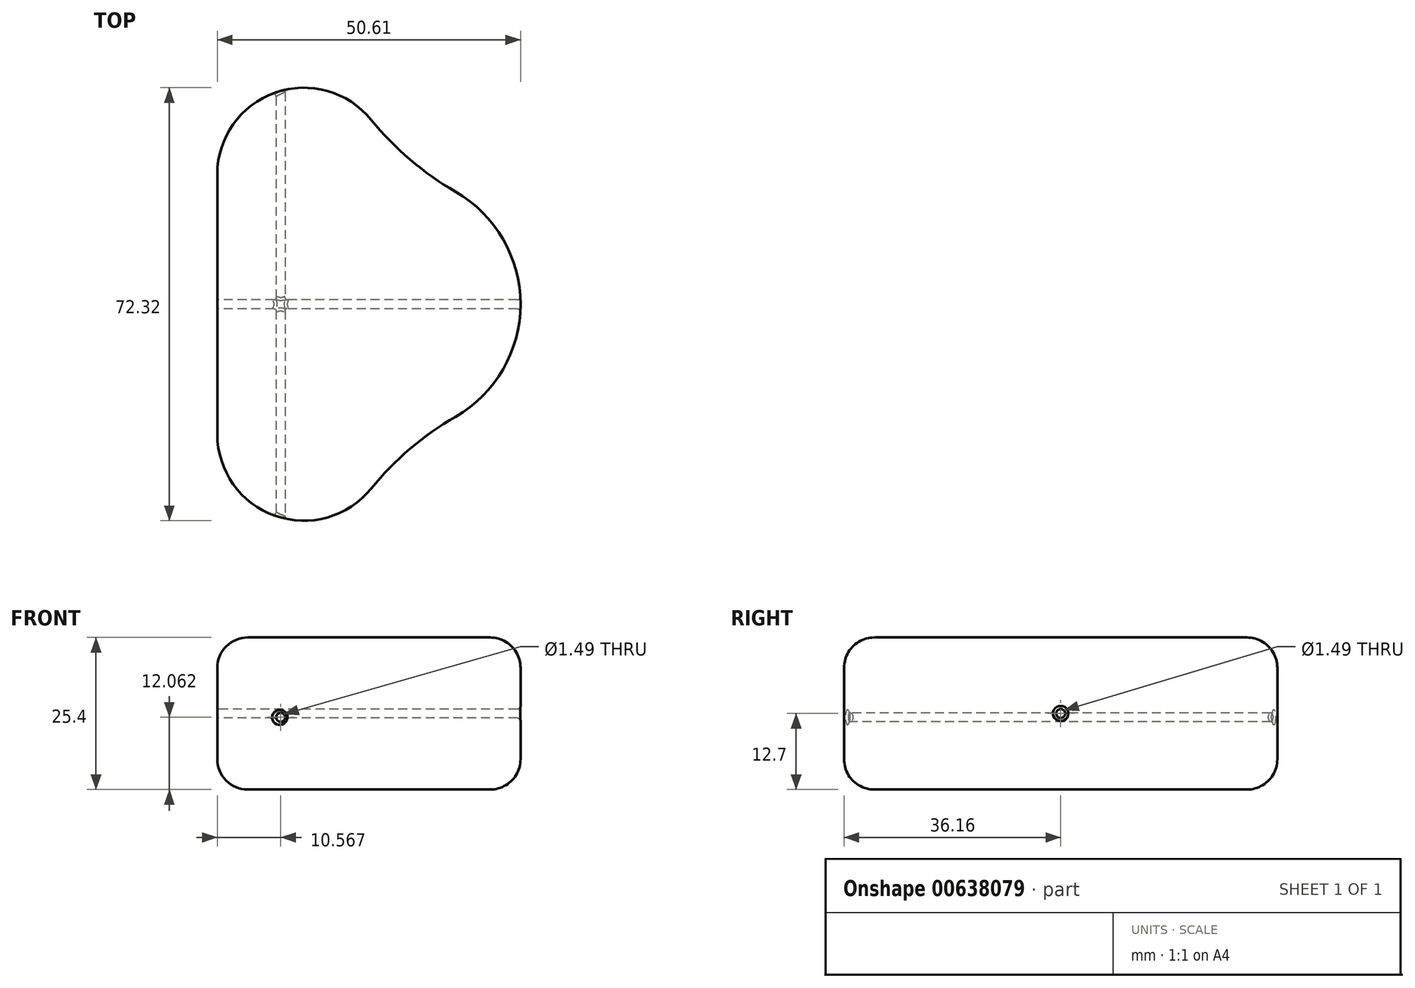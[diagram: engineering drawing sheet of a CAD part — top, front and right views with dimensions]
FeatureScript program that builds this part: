
annotation { "Feature Type Name" : "Feature", "Feature Type Description" : "" }
export const myFeature = defineFeature(function(context is Context, id is Id, definition is map)
    precondition{}
    {
        {
            var Q0;
            Q0=qCreatedBy(makeId("Top.planeOp"),FACE);
            var sketch = newSketch(context, id + "F0", { "sketchPlane" : qUnion([Q0])});
            skLineSegment(sketch, "E0.bottom", {"start": v(-14.45, -21.7) * mm, "end": v(14.45, -21.7) * mm});
            skLineSegment(sketch, "E0.top", {"start": v(-14.45, 21.7) * mm, "end": v(14.45, 21.7) * mm});
            skLineSegment(sketch, "E0.left", {"start": v(-14.45, -21.7) * mm, "end": v(-14.45, 21.7) * mm});
            skLineSegment(sketch, "E0.right", {"start": v(14.45, -21.7) * mm, "end": v(14.45, 21.7) * mm});
            skPoint(sketch, "E0.middle", {"position": v(0, 0) * mm});
            skCircle(sketch, "E1", {"center": v(0, -21.7) * mm, "radius": 14.45 * mm});
            skCircle(sketch, "E2", {"center": v(0, 21.7) * mm, "radius": 14.45 * mm});
            skCircle(sketch, "E3", {"center": v(14.45, 0) * mm, "radius": 21.7 * mm});
            skSolve(sketch);
        }
        {
            var Q0;
            {var subQ0=sQuery(id+"F0.wireOp",EDGE,"E0.top");Q0=makeQuery(id+"F0.imprint","IMPRINT",FACE,{"disambiguationData":[TD([[makeQuery(id+"F0.imprint","IMPRINT",EDGE,{"derivedFrom":subQ0}),1.0]])]});}
            var Q1;
            {var subQ0=sQuery(id+"F0.wireOp",EDGE,"E0.top");Q1=makeQuery(id+"F0.imprint","IMPRINT",FACE,{"disambiguationData":[TD([[makeQuery(id+"F0.imprint","IMPRINT",EDGE,{"derivedFrom":subQ0}),-1.0]])]});}
            var Q2;
            {var subQ0=sQuery(id+"F0.wireOp",EDGE,"E3");var subQ1=sQuery(id+"F0.wireOp",EDGE,"E2");var subQ3=makeQuery(id+"F0.imprint","INTERSECT",VERTEX,{"derivedFrom":[subQ1,subQ0]});Q2=makeQuery(id+"F0.imprint","IMPRINT",FACE,{"disambiguationData":[TD([[makeQuery(id+"F0.imprint","IMPRINT",EDGE,{"disambiguationData":[TD([[subQ3,-1.0]])],"derivedFrom":subQ1}),1.0]])]});}
            var Q3;
            {var subQ0=sQuery(id+"F0.wireOp",EDGE,"E0.left");Q3=makeQuery(id+"F0.imprint","IMPRINT",FACE,{"disambiguationData":[TD([[makeQuery(id+"F0.imprint","IMPRINT",EDGE,{"derivedFrom":subQ0}),-1.0]])]});}
            var Q4;
            {var subQ0=sQuery(id+"F0.wireOp",EDGE,"E0.bottom");Q4=makeQuery(id+"F0.imprint","IMPRINT",FACE,{"disambiguationData":[TD([[makeQuery(id+"F0.imprint","IMPRINT",EDGE,{"derivedFrom":subQ0}),1.0]])]});}
            var Q5;
            {var subQ0=sQuery(id+"F0.wireOp",EDGE,"E0.right");Q5=makeQuery(id+"F0.imprint","IMPRINT",FACE,{"disambiguationData":[TD([[makeQuery(id+"F0.imprint","IMPRINT",EDGE,{"derivedFrom":subQ0}),1.0]])]});}
            var Q6;
            {var subQ0=sQuery(id+"F0.wireOp",EDGE,"E0.right");Q6=makeQuery(id+"F0.imprint","IMPRINT",FACE,{"disambiguationData":[TD([[makeQuery(id+"F0.imprint","IMPRINT",EDGE,{"derivedFrom":subQ0}),-1.0]])]});}
            var Q7;
            {var subQ0=sQuery(id+"F0.wireOp",EDGE,"E0.bottom");Q7=makeQuery(id+"F0.imprint","IMPRINT",FACE,{"disambiguationData":[TD([[makeQuery(id+"F0.imprint","IMPRINT",EDGE,{"derivedFrom":subQ0}),-1.0]])]});}
            var Q8;
            {var subQ0=sQuery(id+"F0.wireOp",EDGE,"E3");var subQ1=sQuery(id+"F0.wireOp",EDGE,"E1");var subQ3=makeQuery(id+"F0.imprint","INTERSECT",VERTEX,{"derivedFrom":[subQ1,subQ0]});Q8=makeQuery(id+"F0.imprint","IMPRINT",FACE,{"disambiguationData":[TD([[makeQuery(id+"F0.imprint","IMPRINT",EDGE,{"disambiguationData":[TD([[subQ3,1.0]])],"derivedFrom":subQ1}),1.0]])]});}
            extrude(context, id + "F1", {"entities" : qUnion([Q0, Q1, Q2, Q3, Q4, Q5, Q6, Q7, Q8]), "depth" : 25.4 * mm, "offsetDistance" : 25.4 * mm});
        }
        {
            var Q0;
            Q0=makeQuery(id+"F1.opExtrude","SWEPT_EDGE",EDGE,{"disambiguationData":[OSD([sQuery(id+"F0.wireOp",EDGE,"E0.top"),sQuery(id+"F0.wireOp",EDGE,"E0.right"),sQuery(id+"F0.wireOp",EDGE,"E2"),sQuery(id+"F0.wireOp",EDGE,"E3")])]});
            var Q1;
            Q1=makeQuery(id+"F1.opExtrude","SWEPT_EDGE",EDGE,{"disambiguationData":[OSD([sQuery(id+"F0.wireOp",EDGE,"E0.bottom"),sQuery(id+"F0.wireOp",EDGE,"E0.right"),sQuery(id+"F0.wireOp",EDGE,"E1"),sQuery(id+"F0.wireOp",EDGE,"E3")])]});
            fillet(context, id + "F2", {"entities" : qUnion([Q0, Q1]), "radius" : 50.8 * mm, "tangentPropagation" : true, "allowEdgeOverflow" : false});
        }
        {
            var Q0;
            Q0=makeQuery(id+"F1.opExtrude","CAP_EDGE",EDGE,{"disambiguationData":[OSD([sQuery(id+"F0.wireOp",EDGE,"E1")])],"isStart":false});
            var Q1;
            Q1=makeQuery(id+"F1.opExtrude","CAP_EDGE",EDGE,{"disambiguationData":[OSD([sQuery(id+"F0.wireOp",EDGE,"E0.left")])],"isStart":true});
            fillet(context, id + "F3", {"entities" : qUnion([Q0, Q1]), "radius" : 5.08 * mm, "tangentPropagation" : true, "allowEdgeOverflow" : false});
        }
        {
            var Q0;
            Q0=qCreatedBy(makeId("Front.planeOp"),FACE);
            var sketch = newSketch(context, id + "F4", { "sketchPlane" : qUnion([Q0])});
            skCircle(sketch, "E4", {"center": v(-3.88, 12.06) * mm, "radius": 0.75 * mm});
            skSolve(sketch);
        }
        {
            var Q0;
            Q0 = qSketchRegion(id + "F4", true);
            extrude(context, id + "F5", {"entities" : qUnion([Q0]), "operationType" : NewBodyOperationType.REMOVE, "endBound" : BoundingType.SYMMETRIC, "oppositeDirection" : true, "depth" : 76.2 * mm, "offsetDistance" : 25.4 * mm});
        }
        {
            var Q0;
            Q0=makeQuery(id+"F1.opExtrude","SWEPT_FACE",FACE,{"disambiguationData":[OSD([sQuery(id+"F0.wireOp",EDGE,"E0.left")])]});
            var sketch = newSketch(context, id + "F6", { "sketchPlane" : qUnion([Q0])});
            skCircle(sketch, "E5", {"center": v(0, 12.7) * mm, "radius": 0.75 * mm});
            skPoint(sketch, "E5.centerSnap0", {"position": v(-21.7, 12.7) * mm});
            skPoint(sketch, "E5.centerSnap1", {"position": v(0, 5.08) * mm});
            skSolve(sketch);
        }
        {
            var Q0;
            Q0=makeQuery(id+"F6.imprint","IMPRINT",FACE,{"disambiguationData":[TD([[makeQuery(id+"F6.imprint","IMPRINT",EDGE,{"derivedFrom":sQuery(id+"F6.wireOp",EDGE,"E5")}),1.0]])]});
            extrude(context, id + "F7", {"entities" : qUnion([Q0]), "operationType" : NewBodyOperationType.REMOVE, "oppositeDirection" : true, "depth" : 76.2 * mm, "offsetDistance" : 25.4 * mm});
        }
        {
            var Q0;
            Q0=makeQuery(id+"F5.boolean.opBoolean","INTERSECT",EDGE,{"derivedFrom":[makeQuery(id+"F1.opExtrude","SWEPT_FACE",FACE,{"disambiguationData":[OSD([sQuery(id+"F0.wireOp",EDGE,"E2")])]}),makeQuery(id+"F5.opExtrude","SWEPT_FACE",FACE,{"disambiguationData":[OSD([sQuery(id+"F4.wireOp",EDGE,"E4")])]})]});
            var Q1;
            Q1=makeQuery(id+"F5.boolean.opBoolean","INTERSECT",EDGE,{"derivedFrom":[makeQuery(id+"F1.opExtrude","SWEPT_FACE",FACE,{"disambiguationData":[OSD([sQuery(id+"F0.wireOp",EDGE,"E1")])]}),makeQuery(id+"F5.opExtrude","SWEPT_FACE",FACE,{"disambiguationData":[OSD([sQuery(id+"F4.wireOp",EDGE,"E4")])]})]});
            var Q2;
            Q2=makeQuery(id+"F7.boolean.opBoolean","COPY",EDGE,{"derivedFrom":makeQuery(id+"F7.opExtrude","CAP_EDGE",EDGE,{"disambiguationData":[OSD([sQuery(id+"F6.wireOp",EDGE,"E5")])],"isStart":true})});
            var Q3;
            Q3=makeQuery(id+"F7.boolean.opBoolean","INTERSECT",EDGE,{"derivedFrom":[makeQuery(id+"F1.opExtrude","SWEPT_FACE",FACE,{"disambiguationData":[OSD([sQuery(id+"F0.wireOp",EDGE,"E3")])]}),makeQuery(id+"F7.opExtrude","SWEPT_FACE",FACE,{"disambiguationData":[OSD([sQuery(id+"F6.wireOp",EDGE,"E5")])]})]});
            var Q4;
            Q4=makeQuery(id+"F7.boolean.opBoolean","INTERSECT",EDGE,{"derivedFrom":[makeQuery(id+"F5.boolean.opBoolean","COPY",FACE,{"derivedFrom":makeQuery(id+"F5.opExtrude","SWEPT_FACE",FACE,{"disambiguationData":[OSD([sQuery(id+"F4.wireOp",EDGE,"E4")])]})}),makeQuery(id+"F7.opExtrude","SWEPT_FACE",FACE,{"disambiguationData":[OSD([sQuery(id+"F6.wireOp",EDGE,"E5")])]})]});
            fillet(context, id + "F8", {"entities" : qUnion([Q0, Q1, Q2, Q3, Q4]), "radius" : 0.5 * mm, "tangentPropagation" : true, "allowEdgeOverflow" : false});
        }
    });
